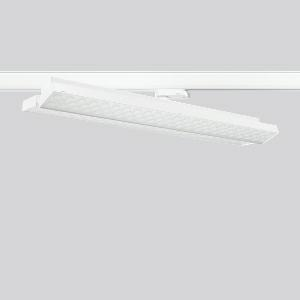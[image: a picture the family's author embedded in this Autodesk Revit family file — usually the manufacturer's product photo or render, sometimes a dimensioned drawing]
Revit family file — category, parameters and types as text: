
# Revit family: tx-move_742162_002_3_de47
name_source: partatom
category: Lighting Fixtures
units: mm (PartAtom-declared; Revit-internal decimal feet)

## family parameters
Cut with Voids When Loaded = No
Host = Face
Light Source = No
Part Type = Normal
Room Calculation Point = No
Round Connector Dimension = Use Diameter
Shared = No

## types (1)
- MultiLumen 1 (1 x LED Modul 835, 3050 lm, 3500)
    Apparent Load = 41 VA
    CIE Flux Codes = 77 96 99 100 100
    Color Rendering = 80
    Color Temperature = 3500
    Default Elevation = 1800 mm
    Description = Series: TX-MOVE
Multifunctional surface-mounted spotlight for area lighting. Very flat design. Housing: sheet steel, powder-coated. Rotation range: 356°. Swivel range: 90°. Consistent alignment possible with visible tilt scale. High-efficiency LED units with optimum light control thanks to clear plastic (PC) lens optics. Spezielle Mikrostrukturen reduzieren Gelbsaum. Symmetrical light distribution. With multi adaptor for 3-circuit tracks 230 V. Suitable for Track on ceiling. MultiLumen: Luminous flux adjustable in 3 steps. Factory setting is the highest luminous flux. Environmentally friendly and resource-saving due to replaceable and recyclable components. 
Colour: traffic white, matt (RAL 9016)
Length: 570 mm
Width: 119 mm
Height: 92 mm
Lamp: LED
Socket: without socket
Colour temperature: 3500K
Colour rendering index (CRI): 80
System power: 41 W
Rated luminous flux: 6100 lm
Luminous efficiency: 149 lm/W
System power 2: 57 W
Rated luminous flux 2: 8300 lm
Luminous efficiency 2: 146 lm/W
System power 3: 73 W
Rated luminous flux 3: 10200 lm
Luminous efficiency 3: 140 lm/W
Control gear: Regulated power supply
Protection class: I
Type of protection: IP 20
    Height = 75 mm
    Lamp = 1 x LED Modul 835
    Lamp Light Flux = 3050 lm
    Lamp count = 1
    Length = 569 mm
    Lifetime = 50000 h
    Luminous efficacy = 149 lm/W
    Manufacturer = RZB
    ModVariant = No
    Model = 742162.002.3
    Mounting Place = Ceiling
    Mounting Type = Rail mounted
    Number of Poles = 1
    OnlyDefault = Yes
    Power Factor = 1
    Product Name = TX-MOVE
    Product group = Track mounted projectors
    ProductGroupID = 301
    Protection Class = Protection class I
    Protection Degree = IP 20
    RLX_Detail_Level = 1
    RLX_Emergency_Light_Flux = 0 lm
    RLX_Emergency_Type = 0
    RLX_Emergency_Type_DB = No
    RlxData = <blob elided: 31081 chars, md5=8d3a3d47>
    Socket = socket
    Standby Power = 0 W
    System Light Flux = 6100 lm
    System Power = 41 W
    Type Comments = MultiLumen 1
    Type Image = 742162.002.jpg
    URL = http://relux.com
    VarID = multilumen_1
    Voltage = 230 V
    Voltage Range = 220-240 V
    Weight = 0.00 kg
    Width = 119 mm

## geometry (parser evidence)
native form markers: Blend x4, Sweep x16
no freeform markers — native parametric forms only
